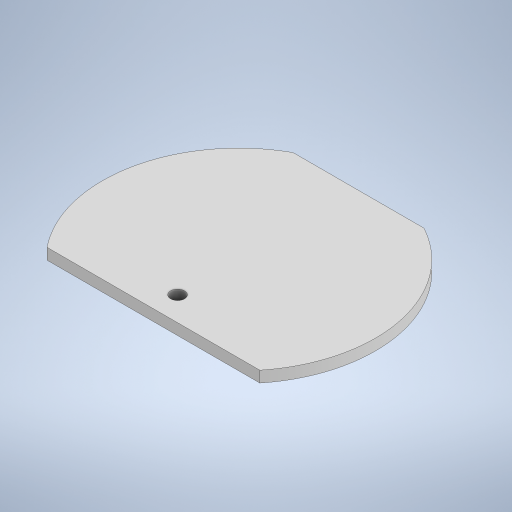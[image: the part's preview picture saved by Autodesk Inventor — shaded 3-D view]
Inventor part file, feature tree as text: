
AUTODESK INVENTOR PART (.ipt)
format: ipt  version: 2024 (Build 280153000, 153)  size: 226,304 bytes
history: native  units: mm
features: sketch x3, extrude x2, other x1, mirror x1
ambient origin geometry x8: Origin, YZ Plane, XZ Plane, XY Plane, X Axis, Y Axis, Z Axis, Center Point
bodies: Body1 (feature_tree)
feature tree (7):
  other  "ソリッド1"
  sketch  "スケッチ1"
  extrude  "押し出し1"  Depth=21.5mm
  extrude  "押し出し2"  Depth=15.335mm
  mirror  "ミラー2"
  sketch  "スケッチ2"
  sketch  "スケッチ3"
